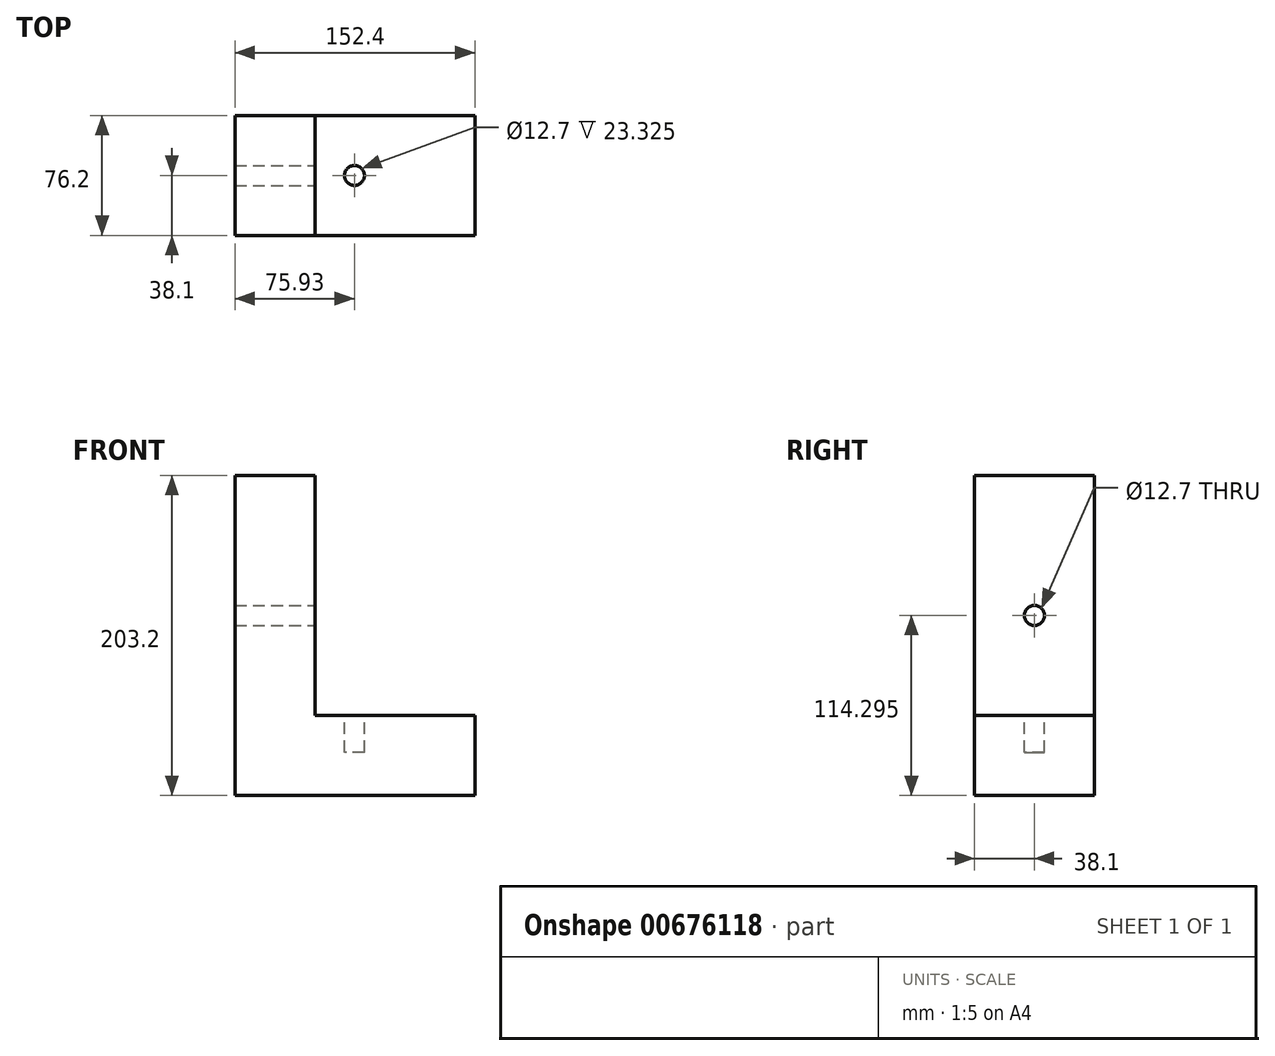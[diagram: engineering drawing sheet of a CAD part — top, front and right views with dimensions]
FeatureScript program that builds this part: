
annotation { "Feature Type Name" : "Feature", "Feature Type Description" : "" }
export const myFeature = defineFeature(function(context is Context, id is Id, definition is map)
    precondition{}
    {
        {
            var Q0;
            Q0=qCreatedBy(makeId("Front.planeOp"),FACE);
            var sketch = newSketch(context, id + "F0", { "sketchPlane" : qUnion([Q0])});
            skLineSegment(sketch, "E0", {"start": v(-75.93, 99.53) * mm, "end": v(-75.93, -103.67) * mm});
            skLineSegment(sketch, "E1", {"start": v(-75.93, -103.67) * mm, "end": v(76.47, -103.67) * mm});
            skLineSegment(sketch, "E2", {"start": v(76.47, -103.67) * mm, "end": v(76.47, -52.87) * mm});
            skLineSegment(sketch, "E3", {"start": v(-75.93, 99.53) * mm, "end": v(-25.13, 99.53) * mm});
            skLineSegment(sketch, "E4", {"start": v(-25.13, 99.53) * mm, "end": v(-25.13, -52.87) * mm});
            skLineSegment(sketch, "E5", {"start": v(-25.13, -52.87) * mm, "end": v(76.47, -52.87) * mm});
            skSolve(sketch);
        }
        {
            var Q0;
            Q0 = qSketchRegion(id + "F0", true);
            extrude(context, id + "F1", {"entities" : qUnion([Q0]), "depth" : 76.2 * mm, "offsetDistance" : 25.4 * mm});
        }
        {
            var Q0;
            Q0=qCreatedBy(makeId("Right.planeOp"),FACE);
            var sketch = newSketch(context, id + "F2", { "sketchPlane" : qUnion([Q0])});
            skCircle(sketch, "E6", {"center": v(-38.1, 10.63) * mm, "radius": 6.35 * mm});
            skSolve(sketch);
        }
        {
            var Q0;
            Q0=makeQuery(id+"F2.imprint","IMPRINT",FACE,{"disambiguationData":[TD([[makeQuery(id+"F2.imprint","IMPRINT",EDGE,{"derivedFrom":sQuery(id+"F2.wireOp",EDGE,"E6")}),1.0]])]});
            extrude(context, id + "F3", {"entities" : qUnion([Q0]), "operationType" : NewBodyOperationType.REMOVE, "oppositeDirection" : true, "depth" : 76.2 * mm, "offsetDistance" : 25.4 * mm});
        }
        {
            var Q0;
            Q0=qCreatedBy(makeId("Top.planeOp"),FACE);
            var sketch = newSketch(context, id + "F4", { "sketchPlane" : qUnion([Q0])});
            skCircle(sketch, "E7", {"center": v(0, -38.1) * mm, "radius": 6.35 * mm});
            skSolve(sketch);
        }
        {
            var Q0;
            Q0 = qSketchRegion(id + "F4", true);
            extrude(context, id + "F5", {"entities" : qUnion([Q0]), "operationType" : NewBodyOperationType.REMOVE, "oppositeDirection" : true, "depth" : 76.2 * mm, "offsetDistance" : 25.4 * mm});
        }
    });
